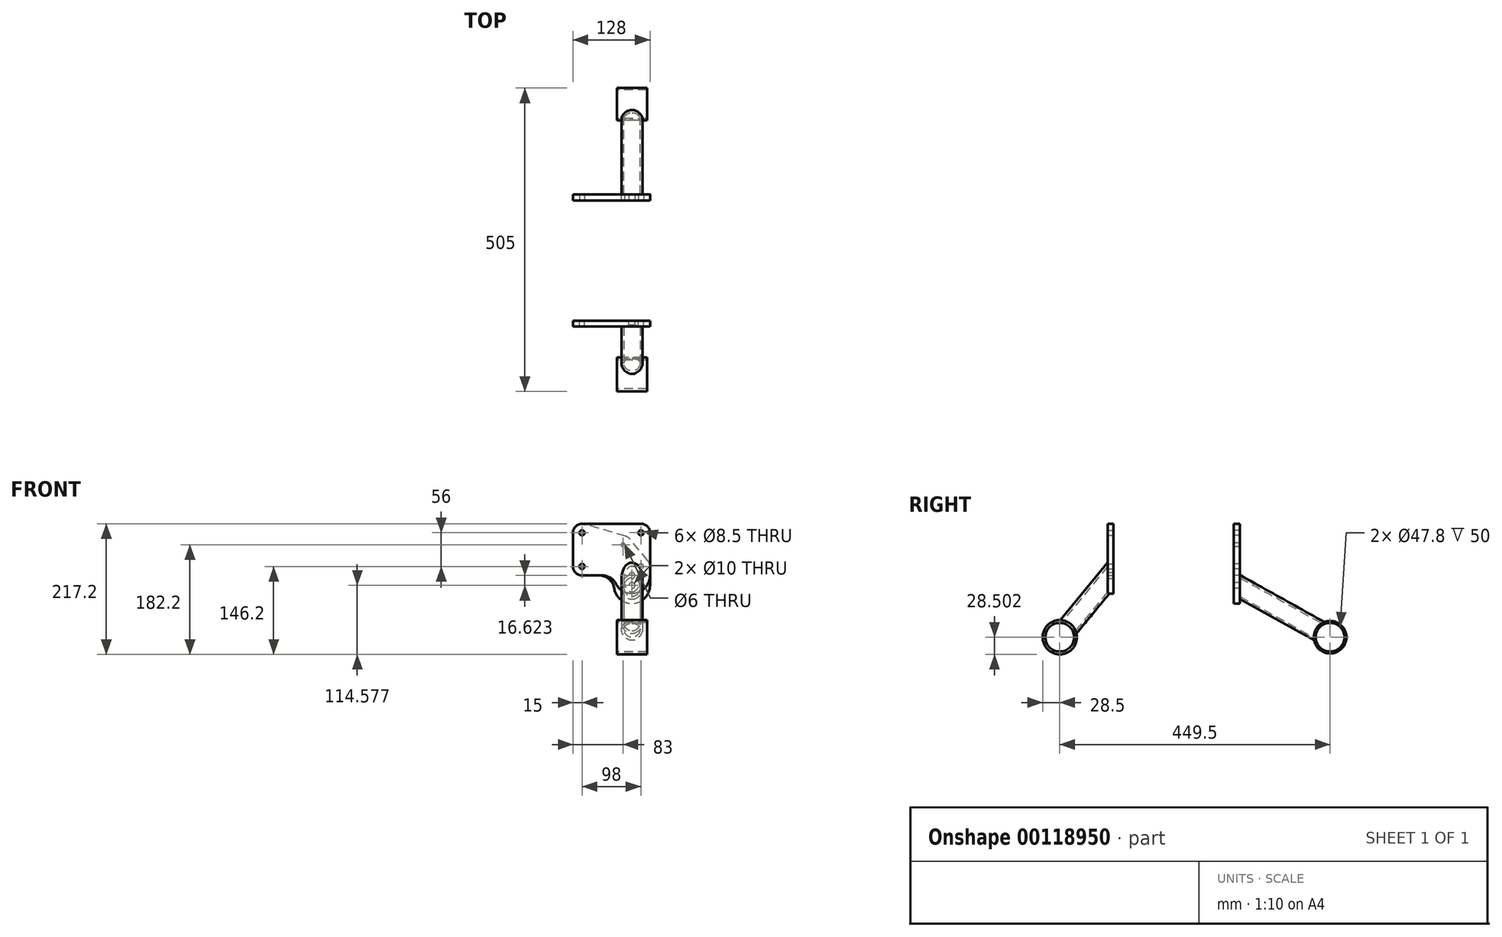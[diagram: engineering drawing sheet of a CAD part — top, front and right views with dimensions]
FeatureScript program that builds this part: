
annotation { "Feature Type Name" : "Feature", "Feature Type Description" : "" }
export const myFeature = defineFeature(function(context is Context, id is Id, definition is map)
    precondition{}
    {
        {
            var Q0;
            Q0=qCreatedBy(makeId("Front.planeOp"),FACE);
            cPlane(context, id + "F0", {"entities" : qUnion([Q0]), "cplaneType" : CPlaneType.OFFSET, "offset" : 100 * mm, "width" : 150 * mm, "height" : 150 * mm});
        }
        {
            var Q0;
            Q0=qCreatedBy(makeId("Front.planeOp"),FACE);
            cPlane(context, id + "F1", {"entities" : qUnion([Q0]), "cplaneType" : CPlaneType.OFFSET, "offset" : 100 * mm, "oppositeDirection" : true, "width" : 150 * mm, "height" : 150 * mm});
        }
        {
            var Q0;
            Q0=qCreatedBy(id+"F1.planeOp",FACE);
            var sketch = newSketch(context, id + "F2", { "sketchPlane" : qUnion([Q0])});
            skCircle(sketch, "E0", {"center": v(0, 0) * mm, "radius": 4.25 * mm});
            skCircle(sketch, "E1", {"center": v(0, -56) * mm, "radius": 4.25 * mm});
            skCircle(sketch, "E2", {"center": v(98, -56) * mm, "radius": 4.25 * mm});
            skCircle(sketch, "E3", {"center": v(68, -20) * mm, "radius": 3 * mm});
            skCircle(sketch, "E4", {"center": v(83, -87.62) * mm, "radius": 5 * mm});
            skArc(sketch, "E5", {"start": v(53.35, -92.2) * mm, "mid": v(85.3, -117.54) * mm, "end": v(113, -87.62) * mm});
            skArc(sketch, "E6", {"start": v(79.52, -10.4) * mm, "mid": v(76.23, -7.46) * mm, "end": v(72.23, -5.6) * mm});
            skArc(sketch, "E7", {"start": v(4.23, 14.4) * mm, "mid": v(-8.99, 12.01) * mm, "end": v(-15, 0) * mm});
            skArc(sketch, "E8", {"start": v(-15, -56) * mm, "mid": v(-10.6, -66.6) * mm, "end": v(0, -71) * mm});
            skArc(sketch, "E9", {"start": v(113, -56) * mm, "mid": v(112.1, -50.9) * mm, "end": v(109.52, -46.4) * mm});
            skLineSegment(sketch, "E10", {"start": v(109.52, -46.4) * mm, "end": v(79.52, -10.4) * mm});
            skLineSegment(sketch, "E11", {"start": v(72.23, -5.6) * mm, "end": v(4.23, 14.4) * mm});
            skLineSegment(sketch, "E12", {"start": v(-15, 0) * mm, "end": v(-15, -56) * mm});
            skLineSegment(sketch, "E13", {"start": v(113, -56) * mm, "end": v(113, -87.62) * mm});
            skCircle(sketch, "E14", {"center": v(98, -56) * mm, "radius": 15 * mm, "construction": true});
            skLineSegment(sketch, "E15", {"start": v(28.64, -71) * mm, "end": v(0, -71) * mm});
            skArc(sketch, "E16", {"start": v(53.35, -92.2) * mm, "mid": v(44.92, -77.02) * mm, "end": v(28.64, -71) * mm});
            skCircle(sketch, "E17", {"center": v(83, -87.62) * mm, "radius": 20 * mm, "construction": true});
            skSolve(sketch);
        }
        {
            var Q0;
            Q0=qSketchRegion(id+"F2",true);
            extrude(context, id + "F3", {"entities" : qUnion([Q0]), "oppositeDirection" : true, "depth" : 10 * mm, "offsetDistance" : 25 * mm});
        }
        {
            var Q0;
            Q0=qCreatedBy(id+"F0.planeOp",FACE);
            var sketch = newSketch(context, id + "F4", { "sketchPlane" : qUnion([Q0])});
            skCircle(sketch, "E18", {"center": v(0, 0) * mm, "radius": 4.25 * mm});
            skCircle(sketch, "E19", {"center": v(0, -56) * mm, "radius": 4.25 * mm});
            skCircle(sketch, "E20", {"center": v(98, 0) * mm, "radius": 4.25 * mm});
            skArc(sketch, "E21", {"start": v(0, 15) * mm, "mid": v(-10.6, 10.6) * mm, "end": v(-15, 0) * mm});
            skArc(sketch, "E22", {"start": v(-15, -56) * mm, "mid": v(-10.6, -66.6) * mm, "end": v(0, -71) * mm});
            skArc(sketch, "E23", {"start": v(113, 0) * mm, "mid": v(108.6, 10.6) * mm, "end": v(98, 15) * mm});
            skLineSegment(sketch, "E24", {"start": v(0, 15) * mm, "end": v(98, 15) * mm});
            skLineSegment(sketch, "E25", {"start": v(-15, -56) * mm, "end": v(-15, 0) * mm});
            skCircle(sketch, "E26", {"center": v(83, -71) * mm, "radius": 5 * mm});
            skLineSegment(sketch, "E27", {"start": v(113, -71) * mm, "end": v(113, 0) * mm});
            skLineSegment(sketch, "E28", {"start": v(53, -71) * mm, "end": v(0, -71) * mm});
            skLineSegment(sketch, "E29", {"start": v(83, -71) * mm, "end": v(83, 0.1) * mm, "construction": true});
            skArc(sketch, "E30", {"start": v(53, -71) * mm, "mid": v(83, -101) * mm, "end": v(113, -71) * mm});
            skLineSegment(sketch, "E31", {"start": v(53, -71) * mm, "end": v(148.78, -71) * mm, "construction": true});
            skSolve(sketch);
        }
        {
            var Q0;
            Q0=qSketchRegion(id+"F4",true);
            extrude(context, id + "F5", {"entities" : qUnion([Q0]), "depth" : 10 * mm, "offsetDistance" : 25 * mm});
        }
        {
            var Q0;
            Q0=qCreatedBy(id+"F0.planeOp",FACE);
            cPlane(context, id + "F6", {"entities" : qUnion([Q0]), "cplaneType" : CPlaneType.OFFSET, "offset" : 5 * mm, "width" : 150 * mm, "height" : 150 * mm});
        }
        {
            var Q0;
            Q0=qCreatedBy(id+"F6.planeOp",FACE);
            var sketch = newSketch(context, id + "F7", { "sketchPlane" : qUnion([Q0])});
            skCircle(sketch, "E32.0", {"center": v(83, -71) * mm, "radius": 5 * mm, "construction": true});
            skLineSegment(sketch, "E33", {"start": v(-37.6, -71) * mm, "end": v(222.5, -71) * mm, "construction": true});
            skSolve(sketch);
        }
        {
            var Q0;
            Q0=makeQuery(id+"F3.opExtrude","CAP_FACE",FACE,{"disambiguationData":[OSD([sQuery(id+"F2.wireOp",EDGE,"E0"),sQuery(id+"F2.wireOp",EDGE,"E1"),sQuery(id+"F2.wireOp",EDGE,"E2"),sQuery(id+"F2.wireOp",EDGE,"E3"),sQuery(id+"F2.wireOp",EDGE,"E4"),sQuery(id+"F2.wireOp",EDGE,"E5"),sQuery(id+"F2.wireOp",EDGE,"E6"),sQuery(id+"F2.wireOp",EDGE,"E7"),sQuery(id+"F2.wireOp",EDGE,"E8"),sQuery(id+"F2.wireOp",EDGE,"E9"),sQuery(id+"F2.wireOp",EDGE,"E10"),sQuery(id+"F2.wireOp",EDGE,"E11"),sQuery(id+"F2.wireOp",EDGE,"E12"),sQuery(id+"F2.wireOp",EDGE,"E13"),sQuery(id+"F2.wireOp",EDGE,"E15"),sQuery(id+"F2.wireOp",EDGE,"E16")])],"isStart":false});
            cPlane(context, id + "F8", {"entities" : qUnion([Q0]), "cplaneType" : CPlaneType.OFFSET, "offset" : 5 * mm, "oppositeDirection" : true, "width" : 150 * mm, "height" : 150 * mm});
        }
        {
            var Q0;
            Q0=qCreatedBy(id+"F8.planeOp",FACE);
            var sketch = newSketch(context, id + "F9", { "sketchPlane" : qUnion([Q0])});
            skCircle(sketch, "E34.0", {"center": v(-83, -87.62) * mm, "radius": 5 * mm, "construction": true});
            skLineSegment(sketch, "E35", {"start": v(-157.06, -87.62) * mm, "end": v(53.65, -87.62) * mm, "construction": true});
            skSolve(sketch);
        }
        {
            var Q0;
            Q0=qCreatedBy(makeId("Right.planeOp"),FACE);
            cPlane(context, id + "F10", {"entities" : qUnion([Q0]), "cplaneType" : CPlaneType.OFFSET, "offset" : 83 * mm, "width" : 150 * mm, "height" : 150 * mm});
        }
        {
            var Q0;
            Q0=qCreatedBy(id+"F10.planeOp",FACE);
            var sketch = newSketch(context, id + "F11", { "sketchPlane" : qUnion([Q0])});
            skCircle(sketch, "E36", {"center": v(260, -173.7) * mm, "radius": 27 * mm});
            skCircle(sketch, "E37", {"center": v(260, -173.7) * mm, "radius": 23.9 * mm});
            skCircle(sketch, "E38", {"center": v(-189.5, -173.7) * mm, "radius": 28.5 * mm});
            skCircle(sketch, "E39", {"center": v(-189.5, -173.7) * mm, "radius": 23.9 * mm});
            skLineSegment(sketch, "E40.0", {"start": v(-110, -76) * mm, "end": v(-110, -66) * mm, "construction": true});
            skPoint(sketch, "E41", {"position": v(-110, -71) * mm});
            skLineSegment(sketch, "E42", {"start": v(-189.5, -173.7) * mm, "end": v(-110, -71) * mm, "construction": true});
            skSolve(sketch);
        }
        {
            var Q0;
            Q0=qCreatedBy(id+"F10.planeOp",FACE);
            var sketch = newSketch(context, id + "F12", { "sketchPlane" : qUnion([Q0])});
            skPoint(sketch, "E43.0", {"position": v(-189.5, -173.7) * mm});
            skPoint(sketch, "E44.0", {"position": v(-105, -71) * mm});
            skLineSegment(sketch, "E45", {"start": v(-189.5, -173.7) * mm, "end": v(-105, -71) * mm, "construction": true});
            skPoint(sketch, "E46.0", {"position": v(105, -87.62) * mm});
            skPoint(sketch, "E47.0", {"position": v(260, -173.7) * mm});
            skLineSegment(sketch, "E48", {"start": v(260, -173.7) * mm, "end": v(105, -87.62) * mm, "construction": true});
            skPoint(sketch, "E49", {"position": v(-147.25, -122.35) * mm});
            skPoint(sketch, "E50", {"position": v(182.5, -130.66) * mm});
            skSolve(sketch);
        }
        {
            var Q0;
            Q0=makeQuery(id+"F11.imprint","IMPRINT",FACE,{"disambiguationData":[TD([[makeQuery(id+"F11.imprint","IMPRINT",EDGE,{"derivedFrom":sQuery(id+"F11.wireOp",EDGE,"E36")}),1.0]])]});
            var Q1;
            Q1=makeQuery(id+"F11.imprint","IMPRINT",FACE,{"disambiguationData":[TD([[makeQuery(id+"F11.imprint","IMPRINT",EDGE,{"derivedFrom":sQuery(id+"F11.wireOp",EDGE,"E38")}),1.0]])]});
            extrude(context, id + "F13", {"entities" : qUnion([Q0, Q1]), "depth" : 50 * mm, "offsetDistance" : 25 * mm, "symmetric" : true});
        }
        {
            var Q0;
            Q0=sQuery(id+"F12.wireOp",VERTEX,"E49");
            var Q1;
            Q1=sQuery(id+"F12.wireOp",EDGE,"E45");
            cPlane(context, id + "F14", {"entities" : qUnion([Q0, Q1]), "cplaneType" : CPlaneType.LINE_POINT, "offset" : 25 * mm, "width" : 150 * mm, "height" : 150 * mm});
        }
        {
            var Q0;
            Q0=sQuery(id+"F12.wireOp",VERTEX,"E50");
            var Q1;
            Q1=sQuery(id+"F12.wireOp",EDGE,"E48");
            cPlane(context, id + "F15", {"entities" : qUnion([Q0, Q1]), "cplaneType" : CPlaneType.LINE_POINT, "offset" : 25 * mm, "width" : 150 * mm, "height" : 150 * mm});
        }
        {
            var Q0;
            Q0=qCreatedBy(id+"F15.planeOp",FACE);
            var sketch = newSketch(context, id + "F16", { "sketchPlane" : qUnion([Q0])});
            skPoint(sketch, "E51.0", {"position": v(83, -25.63) * mm});
            skCircle(sketch, "E52", {"center": v(83, -25.63) * mm, "radius": 17.5 * mm});
            skCircle(sketch, "E53", {"center": v(83, -25.63) * mm, "radius": 13.5 * mm});
            skSolve(sketch);
        }
        {
            var Q0;
            Q0=qSketchRegion(id+"F16",true);
            var Q1;
            Q1=makeQuery(id+"F3.opExtrude","SWEPT_BODY",BODY,{"disambiguationData":[OSD([sQuery(id+"F2.wireOp",EDGE,"E0"),sQuery(id+"F2.wireOp",EDGE,"E1"),sQuery(id+"F2.wireOp",EDGE,"E2"),sQuery(id+"F2.wireOp",EDGE,"E3"),sQuery(id+"F2.wireOp",EDGE,"E4"),sQuery(id+"F2.wireOp",EDGE,"E5"),sQuery(id+"F2.wireOp",EDGE,"E6"),sQuery(id+"F2.wireOp",EDGE,"E7"),sQuery(id+"F2.wireOp",EDGE,"E8"),sQuery(id+"F2.wireOp",EDGE,"E9"),sQuery(id+"F2.wireOp",EDGE,"E10"),sQuery(id+"F2.wireOp",EDGE,"E11"),sQuery(id+"F2.wireOp",EDGE,"E12"),sQuery(id+"F2.wireOp",EDGE,"E13"),sQuery(id+"F2.wireOp",EDGE,"E15"),sQuery(id+"F2.wireOp",EDGE,"E16")])]});
            var Q2;
            Q2=makeQuery(id+"F13.opExtrude","SWEPT_BODY",BODY,{"disambiguationData":[OSD([sQuery(id+"F11.wireOp",EDGE,"E36"),sQuery(id+"F11.wireOp",EDGE,"E37")])]});
            extrude(context, id + "F17", {"entities" : qUnion([Q0]), "endBound" : BoundingType.UP_TO_BODY, "depth" : 25 * mm, "endBoundEntityBody" : qUnion([Q1]), "offsetDistance" : 25 * mm, "hasSecondDirection" : true, "secondDirectionBound" : BoundingType.UP_TO_BODY, "secondDirectionOppositeDirection" : true, "secondDirectionDepth" : 25 * mm, "secondDirectionBoundEntityBody" : qUnion([Q2])});
        }
        {
            var Q0;
            Q0=qCreatedBy(id+"F14.planeOp",FACE);
            var sketch = newSketch(context, id + "F18", { "sketchPlane" : qUnion([Q0])});
            skPoint(sketch, "E54.0", {"position": v(83, -35.97) * mm});
            skCircle(sketch, "E55", {"center": v(83, -35.97) * mm, "radius": 17.5 * mm});
            skCircle(sketch, "E56", {"center": v(83, -35.97) * mm, "radius": 13.5 * mm});
            skSolve(sketch);
        }
        {
            var Q0;
            Q0=qSketchRegion(id+"F18",true);
            var Q1;
            Q1=makeQuery(id+"F5.opExtrude","SWEPT_BODY",BODY,{"disambiguationData":[OSD([sQuery(id+"F4.wireOp",EDGE,"E18"),sQuery(id+"F4.wireOp",EDGE,"E19"),sQuery(id+"F4.wireOp",EDGE,"E20"),sQuery(id+"F4.wireOp",EDGE,"E21"),sQuery(id+"F4.wireOp",EDGE,"E22"),sQuery(id+"F4.wireOp",EDGE,"E23"),sQuery(id+"F4.wireOp",EDGE,"E24"),sQuery(id+"F4.wireOp",EDGE,"E25"),sQuery(id+"F4.wireOp",EDGE,"E26"),sQuery(id+"F4.wireOp",EDGE,"vU5l6jaA-Mzrw-TRwD-vVmj-lc8WhW82sC1F"),sQuery(id+"F4.wireOp",EDGE,"E27"),sQuery(id+"F4.wireOp",EDGE,"E28")])]});
            var Q2;
            Q2=makeQuery(id+"F13.opExtrude","SWEPT_BODY",BODY,{"disambiguationData":[OSD([sQuery(id+"F11.wireOp",EDGE,"E38"),sQuery(id+"F11.wireOp",EDGE,"E39")])]});
            extrude(context, id + "F19", {"entities" : qUnion([Q0]), "endBound" : BoundingType.UP_TO_BODY, "depth" : 25 * mm, "endBoundEntityBody" : qUnion([Q1]), "offsetDistance" : 25 * mm, "hasSecondDirection" : true, "secondDirectionBound" : BoundingType.UP_TO_BODY, "secondDirectionOppositeDirection" : true, "secondDirectionDepth" : 25 * mm, "secondDirectionBoundEntityBody" : qUnion([Q2])});
        }
        {
            var Q0;
            Q0=makeQuery(id+"F5.opExtrude","SWEPT_EDGE",EDGE,{"disambiguationData":[OSD([sQuery(id+"F4.wireOp",EDGE,"E28"),sQuery(id+"F4.wireOp",EDGE,"E30")])]});
            fillet(context, id + "F20", {"entities" : qUnion([Q0]), "tangentPropagation" : true, "radius" : 25 * mm, "defaultsChanged" : true, "vertexSettings" : [], "allowEdgeOverflow" : false});
        }
    });
